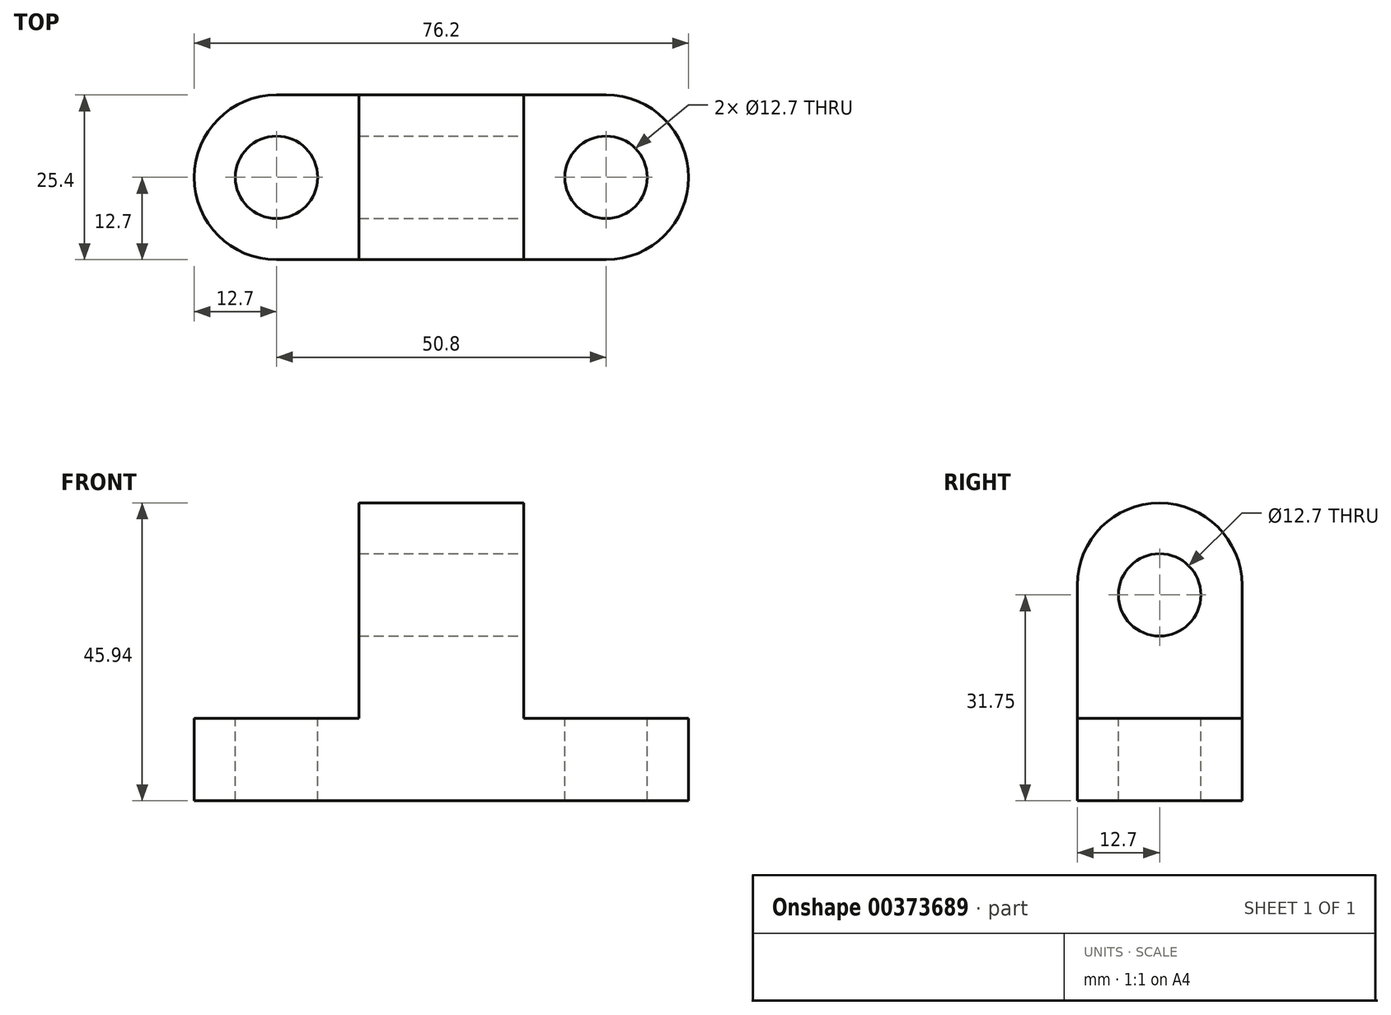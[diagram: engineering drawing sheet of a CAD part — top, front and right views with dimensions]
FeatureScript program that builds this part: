
annotation { "Feature Type Name" : "Feature", "Feature Type Description" : "" }
export const myFeature = defineFeature(function(context is Context, id is Id, definition is map)
    precondition{}
    {
        {
            var Q0;
            Q0=qCreatedBy(makeId("Front.planeOp"),FACE);
            var sketch = newSketch(context, id + "F0", { "sketchPlane" : qUnion([Q0])});
            skLineSegment(sketch, "E0", {"start": v(0, 0) * mm, "end": v(76.2, 0) * mm});
            skLineSegment(sketch, "E1", {"start": v(76.2, 0) * mm, "end": v(76.2, 12.7) * mm});
            skLineSegment(sketch, "E2", {"start": v(76.2, 12.7) * mm, "end": v(50.8, 12.7) * mm});
            skLineSegment(sketch, "E3", {"start": v(50.8, 12.7) * mm, "end": v(50.8, 45.94) * mm});
            skLineSegment(sketch, "E4", {"start": v(50.8, 45.94) * mm, "end": v(25.4, 45.94) * mm});
            skLineSegment(sketch, "E5", {"start": v(25.4, 45.94) * mm, "end": v(25.4, 12.7) * mm});
            skLineSegment(sketch, "E6", {"start": v(25.4, 12.7) * mm, "end": v(0, 12.7) * mm});
            skLineSegment(sketch, "E7", {"start": v(0, 12.7) * mm, "end": v(0, 0) * mm});
            skSolve(sketch);
        }
        {
            var Q0;
            Q0 = qSketchRegion(id + "F0", true);
            extrude(context, id + "F1", {"entities" : qUnion([Q0]), "depth" : 25.4 * mm});
        }
        {
            var Q0;
            Q0=makeQuery(id+"F1.opExtrude","SWEPT_FACE",FACE,{"disambiguationData":[OSD([sQuery(id+"F0.wireOp",EDGE,"E2")])]});
            var sketch = newSketch(context, id + "F2", { "sketchPlane" : qUnion([Q0])});
            skCircle(sketch, "E8", {"center": v(63.5, -12.7) * mm, "radius": 6.35 * mm});
            skPoint(sketch, "E8.centerSnap0", {"position": v(76.2, -12.7) * mm});
            skArc(sketch, "E9", {"start": v(63.5, -25.4) * mm, "mid": v(76.2, -12.7) * mm, "end": v(63.5, 0) * mm});
            skSolve(sketch);
        }
        {
            var Q0;
            Q0=makeQuery(id+"F1.opExtrude","SWEPT_FACE",FACE,{"disambiguationData":[OSD([sQuery(id+"F0.wireOp",EDGE,"E6")])]});
            var sketch = newSketch(context, id + "F3", { "sketchPlane" : qUnion([Q0])});
            skCircle(sketch, "E10", {"center": v(12.7, -12.7) * mm, "radius": 6.35 * mm});
            skPoint(sketch, "E10.centerSnap0", {"position": v(12.7, 0) * mm});
            skPoint(sketch, "E10.centerSnap1", {"position": v(0, -12.7) * mm});
            skArc(sketch, "E11", {"start": v(12.7, 0) * mm, "mid": v(0, -12.7) * mm, "end": v(12.7, -25.4) * mm});
            skSolve(sketch);
        }
        {
            var Q0;
            Q0=makeQuery(id+"F1.opExtrude","SWEPT_FACE",FACE,{"disambiguationData":[OSD([sQuery(id+"F0.wireOp",EDGE,"E3")])]});
            var sketch = newSketch(context, id + "F4", { "sketchPlane" : qUnion([Q0])});
            skCircle(sketch, "E12", {"center": v(-12.7, 31.75) * mm, "radius": 6.35 * mm});
            skPoint(sketch, "E12.centerSnap0", {"position": v(-12.7, 45.94) * mm});
            skArc(sketch, "E13", {"start": v(0, 33.24) * mm, "mid": v(-12.7, 45.94) * mm, "end": v(-25.4, 33.24) * mm});
            skSolve(sketch);
        }
        {
            var Q0;
            {var subQ0=sQuery(id+"F3.wireOp",EDGE,"E11");var subQ1=sQuery(id+"F0.wireOp",EDGE,"E6");var subQ2=makeQuery(id+"F1.opExtrude","CAP_EDGE",EDGE,{"disambiguationData":[OSD([subQ1])],"isStart":true});var subQ3=makeQuery(id+"F3.imprint","INTERSECT",VERTEX,{"derivedFrom":[subQ2,subQ0]});Q0=makeQuery(id+"F3.imprint","IMPRINT",FACE,{"disambiguationData":[TD([[makeQuery(id+"F3.imprint","IMPRINT",EDGE,{"disambiguationData":[TD([[subQ3,-1.0]])],"derivedFrom":subQ0}),-1.0]])]});}
            var Q1;
            Q1=makeQuery(id+"F3.imprint","IMPRINT",FACE,{"disambiguationData":[TD([[makeQuery(id+"F3.imprint","IMPRINT",EDGE,{"derivedFrom":sQuery(id+"F3.wireOp",EDGE,"E10")}),1.0]])]});
            var Q2;
            {var subQ0=sQuery(id+"F3.wireOp",EDGE,"E11");var subQ1=sQuery(id+"F0.wireOp",EDGE,"E6");var subQ2=makeQuery(id+"F1.opExtrude","CAP_EDGE",EDGE,{"disambiguationData":[OSD([subQ1])],"isStart":false});var subQ3=makeQuery(id+"F3.imprint","INTERSECT",VERTEX,{"derivedFrom":[subQ2,subQ0]});Q2=makeQuery(id+"F3.imprint","IMPRINT",FACE,{"disambiguationData":[TD([[makeQuery(id+"F3.imprint","IMPRINT",EDGE,{"disambiguationData":[TD([[subQ3,1.0]])],"derivedFrom":subQ0}),-1.0]])]});}
            var Q3;
            Q3=makeQuery(id+"F2.imprint","IMPRINT",FACE,{"disambiguationData":[TD([[makeQuery(id+"F2.imprint","IMPRINT",EDGE,{"derivedFrom":sQuery(id+"F2.wireOp",EDGE,"E8")}),1.0]])]});
            var Q4;
            {var subQ0=sQuery(id+"F2.wireOp",EDGE,"E9");var subQ1=sQuery(id+"F0.wireOp",EDGE,"E2");var subQ2=makeQuery(id+"F1.opExtrude","CAP_EDGE",EDGE,{"disambiguationData":[OSD([subQ1])],"isStart":true});var subQ3=makeQuery(id+"F2.imprint","INTERSECT",VERTEX,{"derivedFrom":[subQ2,subQ0]});Q4=makeQuery(id+"F2.imprint","IMPRINT",FACE,{"disambiguationData":[TD([[makeQuery(id+"F2.imprint","IMPRINT",EDGE,{"disambiguationData":[TD([[subQ3,1.0]])],"derivedFrom":subQ0}),-1.0]])]});}
            var Q5;
            {var subQ0=sQuery(id+"F2.wireOp",EDGE,"E9");var subQ1=sQuery(id+"F0.wireOp",EDGE,"E2");var subQ2=makeQuery(id+"F1.opExtrude","CAP_EDGE",EDGE,{"disambiguationData":[OSD([subQ1])],"isStart":false});var subQ3=makeQuery(id+"F2.imprint","INTERSECT",VERTEX,{"derivedFrom":[subQ2,subQ0]});Q5=makeQuery(id+"F2.imprint","IMPRINT",FACE,{"disambiguationData":[TD([[makeQuery(id+"F2.imprint","IMPRINT",EDGE,{"disambiguationData":[TD([[subQ3,-1.0]])],"derivedFrom":subQ0}),-1.0]])]});}
            extrude(context, id + "F5", {"entities" : qUnion([Q0, Q1, Q2, Q3, Q4, Q5]), "operationType" : NewBodyOperationType.REMOVE, "oppositeDirection" : true, "depth" : 25.4 * mm});
        }
        {
            var Q0;
            Q0 = qSketchRegion(id + "F4", true);
            var Q1;
            {var subQ0=sQuery(id+"F4.wireOp",EDGE,"E13");var subQ1=sQuery(id+"F0.wireOp",EDGE,"E3");var subQ2=makeQuery(id+"F1.opExtrude","CAP_EDGE",EDGE,{"disambiguationData":[OSD([subQ1])],"isStart":true});var subQ3=makeQuery(id+"F4.imprint","INTERSECT",VERTEX,{"derivedFrom":[subQ2,subQ0]});Q1=makeQuery(id+"F4.imprint","IMPRINT",FACE,{"disambiguationData":[TD([[makeQuery(id+"F4.imprint","IMPRINT",EDGE,{"disambiguationData":[TD([[subQ3,-1.0]])],"derivedFrom":subQ0}),-1.0]])]});}
            var Q2;
            {var subQ0=sQuery(id+"F4.wireOp",EDGE,"E13");var subQ1=sQuery(id+"F0.wireOp",EDGE,"E3");var subQ2=makeQuery(id+"F1.opExtrude","CAP_EDGE",EDGE,{"disambiguationData":[OSD([subQ1])],"isStart":false});var subQ3=makeQuery(id+"F4.imprint","INTERSECT",VERTEX,{"derivedFrom":[subQ2,subQ0]});Q2=makeQuery(id+"F4.imprint","IMPRINT",FACE,{"disambiguationData":[TD([[makeQuery(id+"F4.imprint","IMPRINT",EDGE,{"disambiguationData":[TD([[subQ3,1.0]])],"derivedFrom":subQ0}),-1.0]])]});}
            extrude(context, id + "F6", {"entities" : qUnion([Q0, Q1, Q2]), "operationType" : NewBodyOperationType.REMOVE, "oppositeDirection" : true, "depth" : 25.4 * mm});
        }
    });
